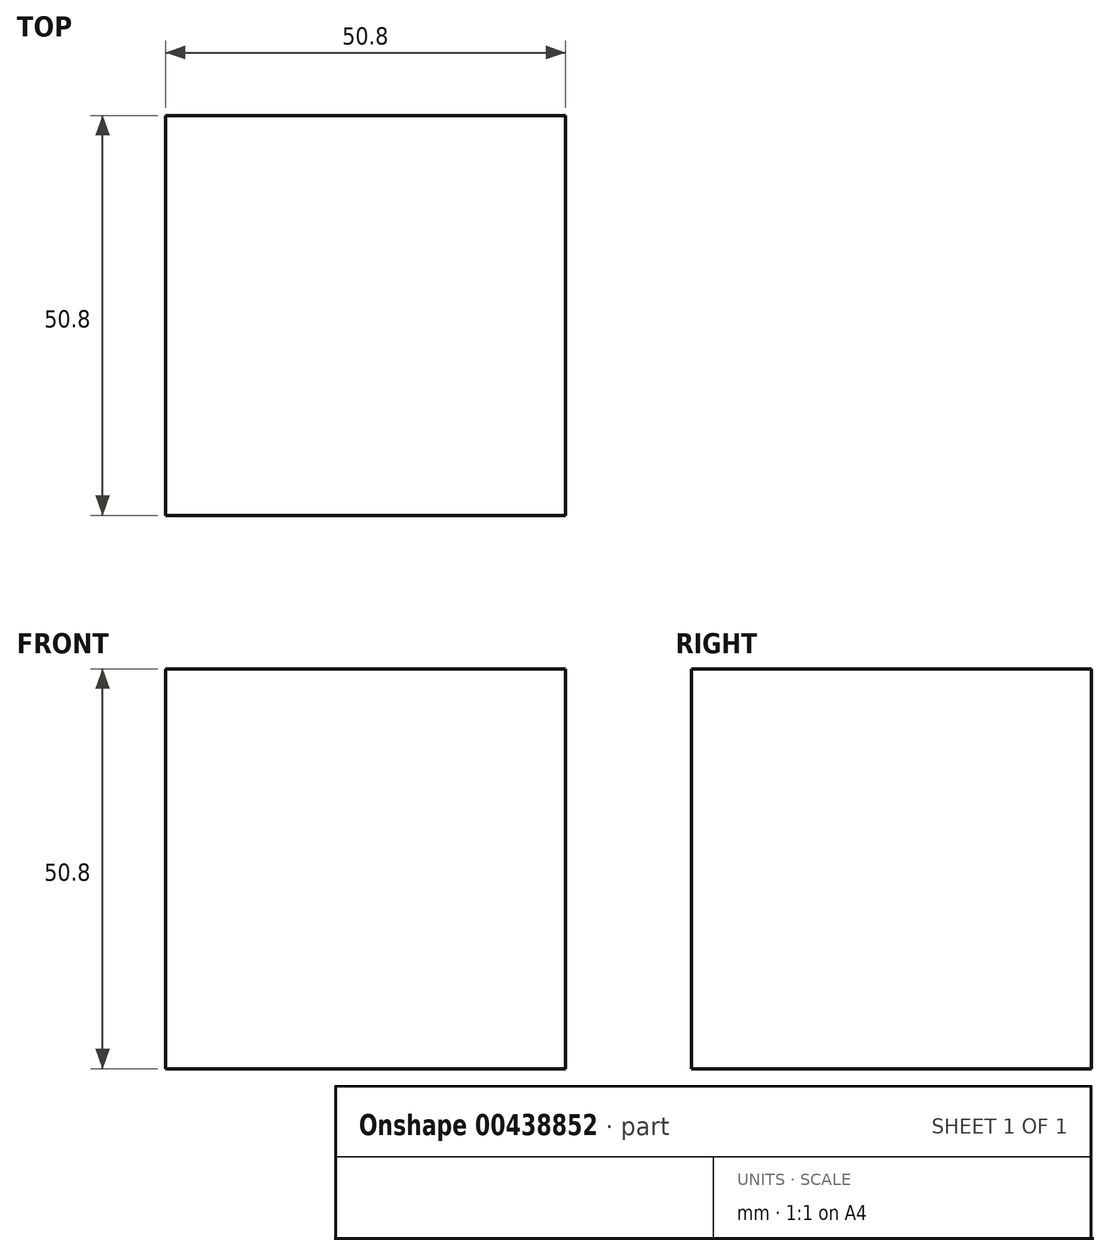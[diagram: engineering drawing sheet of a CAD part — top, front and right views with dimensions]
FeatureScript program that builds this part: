
annotation { "Feature Type Name" : "Feature", "Feature Type Description" : "" }
export const myFeature = defineFeature(function(context is Context, id is Id, definition is map)
    precondition{}
    {
        {
            var Q0;
            Q0=qCreatedBy(makeId("Top.planeOp"),FACE);
            var sketch = newSketch(context, id + "F0", { "sketchPlane" : qUnion([Q0])});
            skLineSegment(sketch, "E0.bottom", {"start": v(25.4, -25.4) * mm, "end": v(-25.4, -25.4) * mm});
            skLineSegment(sketch, "E0.top", {"start": v(25.4, 25.4) * mm, "end": v(-25.4, 25.4) * mm});
            skLineSegment(sketch, "E0.left", {"start": v(25.4, -25.4) * mm, "end": v(25.4, 25.4) * mm});
            skLineSegment(sketch, "E0.right", {"start": v(-25.4, -25.4) * mm, "end": v(-25.4, 25.4) * mm});
            skPoint(sketch, "E0.middle", {"position": v(0, 0) * mm});
            skSolve(sketch);
        }
        {
            var Q0;
            Q0 = qSketchRegion(id + "F0", true);
            extrude(context, id + "F1", {"entities" : qUnion([Q0]), "depth" : 50.8 * mm});
        }
    });
